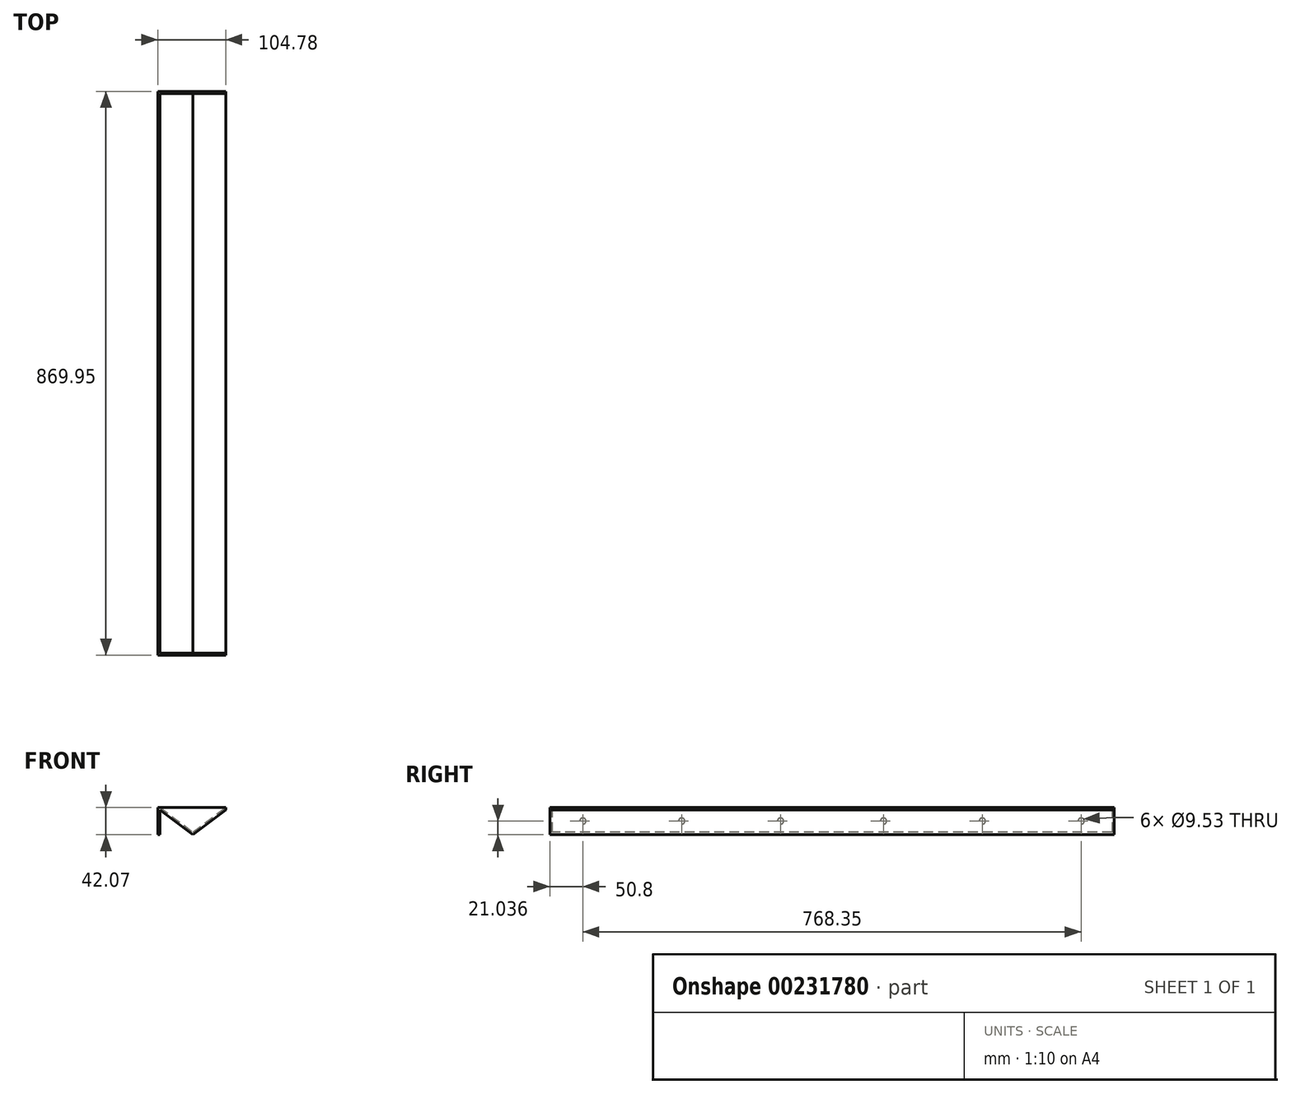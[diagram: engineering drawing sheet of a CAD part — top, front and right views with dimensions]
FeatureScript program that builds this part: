
annotation { "Feature Type Name" : "Feature", "Feature Type Description" : "" }
export const myFeature = defineFeature(function(context is Context, id is Id, definition is map)
    precondition{}
    {
        {
            var Q0;
            Q0=qCreatedBy(makeId("Front.planeOp"),FACE);
            var sketch = newSketch(context, id + "F0", { "sketchPlane" : qUnion([Q0])});
            skLineSegment(sketch, "E0", {"start": v(-50.8, 0) * mm, "end": v(50.8, 0) * mm, "construction": true});
            skLineSegment(sketch, "E1", {"start": v(-50.8, 0) * mm, "end": v(0, -38.1) * mm});
            skLineSegment(sketch, "E2", {"start": v(0, -38.1) * mm, "end": v(50.8, 0) * mm});
            skLineSegment(sketch, "E3", {"start": v(-50.8, 0) * mm, "end": v(-50.8, -42.07) * mm});
            skLineSegment(sketch, "E4", {"start": v(-50.8, -42.07) * mm, "end": v(-53.97, -42.07) * mm});
            skLineSegment(sketch, "E5", {"start": v(-53.97, -42.07) * mm, "end": v(-53.97, 0) * mm});
            skLineSegment(sketch, "E6", {"start": v(-53.97, 0) * mm, "end": v(-50.8, 0) * mm});
            skLineSegment(sketch, "E7.0", {"start": v(-50.8, -3.97) * mm, "end": v(0, -42.07) * mm});
            skLineSegment(sketch, "E8.0", {"start": v(0, -42.07) * mm, "end": v(50.8, -3.97) * mm});
            skLineSegment(sketch, "E9", {"start": v(0, -38.1) * mm, "end": v(0, -46.2) * mm, "construction": true});
            skLineSegment(sketch, "E10", {"start": v(-50.8, 0) * mm, "end": v(-50.8, -3.97) * mm});
            skLineSegment(sketch, "E11", {"start": v(50.8, -3.97) * mm, "end": v(50.8, 0) * mm});
            skLineSegment(sketch, "E12", {"start": v(0, -42.07) * mm, "end": v(-53.97, -42.07) * mm, "construction": true});
            skSolve(sketch);
        }
        {
            var Q0;
            Q0=makeQuery(id+"F0.imprint","IMPRINT",FACE,{"disambiguationData":[TD([[makeQuery(id+"F0.imprint","IMPRINT",EDGE,{"derivedFrom":sQuery(id+"F0.wireOp",EDGE,"E1")}),-1.0]])]});
            var Q1;
            Q1=makeQuery(id+"F0.imprint","IMPRINT",FACE,{"disambiguationData":[TD([[makeQuery(id+"F0.imprint","IMPRINT",EDGE,{"derivedFrom":sQuery(id+"F0.wireOp",EDGE,"E3")}),-1.0]])]});
            extrude(context, id + "F1", {"entities" : qUnion([Q0, Q1]), "oppositeDirection" : true, "depth" : 869.95 * mm});
        }
        {
            var Q0;
            Q0=makeQuery(id+"F1.opExtrude","CAP_FACE",FACE,{"disambiguationData":[OSD([sQuery(id+"F0.wireOp",EDGE,"E1"),sQuery(id+"F0.wireOp",EDGE,"E2"),sQuery(id+"F0.wireOp",EDGE,"E3"),sQuery(id+"F0.wireOp",EDGE,"E4"),sQuery(id+"F0.wireOp",EDGE,"E5"),sQuery(id+"F0.wireOp",EDGE,"E6"),sQuery(id+"F0.wireOp",EDGE,"E7.0"),sQuery(id+"F0.wireOp",EDGE,"E8.0"),sQuery(id+"F0.wireOp",EDGE,"E11")])],"isStart":false});
            var sketch = newSketch(context, id + "F2", { "sketchPlane" : qUnion([Q0])});
            skLineSegment(sketch, "E13", {"start": v(-50.8, 0) * mm, "end": v(50.8, 0) * mm});
            skLineSegment(sketch, "E14", {"start": v(50.8, 0) * mm, "end": v(50.8, -3.97) * mm});
            skLineSegment(sketch, "E15", {"start": v(50.8, -3.97) * mm, "end": v(0, -42.07) * mm});
            skLineSegment(sketch, "E16", {"start": v(0, -42.07) * mm, "end": v(-50.8, -3.97) * mm});
            skLineSegment(sketch, "E17", {"start": v(-50.8, -3.97) * mm, "end": v(-50.8, 0) * mm});
            skSolve(sketch);
        }
        {
            var Q0;
            Q0=makeQuery(id+"F2.imprint","IMPRINT",FACE,{"disambiguationData":[TD([[makeQuery(id+"F2.imprint","IMPRINT",EDGE,{"derivedFrom":sQuery(id+"F2.wireOp",EDGE,"E13")}),-1.0]])]});
            extrude(context, id + "F3", {"entities" : qUnion([Q0]), "operationType" : NewBodyOperationType.ADD, "oppositeDirection" : true, "depth" : 3.17 * mm});
        }
        {
            var Q0;
            Q0=makeQuery(id+"F1.opExtrude","CAP_FACE",FACE,{"disambiguationData":[OSD([sQuery(id+"F0.wireOp",EDGE,"E1"),sQuery(id+"F0.wireOp",EDGE,"E2"),sQuery(id+"F0.wireOp",EDGE,"E3"),sQuery(id+"F0.wireOp",EDGE,"E4"),sQuery(id+"F0.wireOp",EDGE,"E5"),sQuery(id+"F0.wireOp",EDGE,"E6"),sQuery(id+"F0.wireOp",EDGE,"E7.0"),sQuery(id+"F0.wireOp",EDGE,"E8.0"),sQuery(id+"F0.wireOp",EDGE,"E11")])],"isStart":true});
            var sketch = newSketch(context, id + "F4", { "sketchPlane" : qUnion([Q0])});
            skLineSegment(sketch, "E18", {"start": v(-50.8, 0) * mm, "end": v(50.8, 0) * mm});
            skLineSegment(sketch, "E19", {"start": v(50.8, 0) * mm, "end": v(0, -38.1) * mm});
            skLineSegment(sketch, "E20", {"start": v(0, -38.1) * mm, "end": v(-50.8, 0) * mm});
            skSolve(sketch);
        }
        {
            var Q0;
            Q0=makeQuery(id+"F4.imprint","IMPRINT",FACE,{"disambiguationData":[TD([[makeQuery(id+"F4.imprint","IMPRINT",EDGE,{"derivedFrom":sQuery(id+"F4.wireOp",EDGE,"E18")}),-1.0]])]});
            extrude(context, id + "F5", {"entities" : qUnion([Q0]), "operationType" : NewBodyOperationType.ADD, "oppositeDirection" : true, "depth" : 3.17 * mm});
        }
        {
            var Q0;
            Q0=makeQuery(id+"F1.opExtrude","SWEPT_FACE",FACE,{"disambiguationData":[OSD([sQuery(id+"F0.wireOp",EDGE,"E5")])]});
            var sketch = newSketch(context, id + "F6", { "sketchPlane" : qUnion([Q0])});
            skLineSegment(sketch, "E21", {"start": v(-869.95, -21.03) * mm, "end": v(0, -21.03) * mm, "construction": true});
            skCircle(sketch, "E22", {"center": v(-819.15, -21.03) * mm, "radius": 4.76 * mm});
            skLineSegment(sketch, "E23.direction1", {"start": v(-819.15, -21.03) * mm, "end": v(-621.28, -21.03) * mm, "construction": true});
            skCircle(sketch, "E24", {"center": v(-50.8, -21.03) * mm, "radius": 4.76 * mm});
            skLineSegment(sketch, "E25", {"start": v(-434.98, 0) * mm, "end": v(-434.98, -42.07) * mm, "construction": true});
            skCircle(sketch, "E26", {"center": v(-666.75, -21.03) * mm, "radius": 4.76 * mm});
            skCircle(sketch, "E27", {"center": v(-203.2, -21.03) * mm, "radius": 4.76 * mm});
            skCircle(sketch, "E28", {"center": v(-514.35, -21.03) * mm, "radius": 4.76 * mm});
            skCircle(sketch, "E29", {"center": v(-355.6, -21.03) * mm, "radius": 4.76 * mm});
            skSolve(sketch);
        }
        {
            var Q0;
            Q0=sQuery(id+"F6.wireOp",VERTEX,"E22.center");
            var Q1;
            Q1=sQuery(id+"F6.wireOp",VERTEX,"E26.center");
            var Q2;
            Q2=sQuery(id+"F6.wireOp",VERTEX,"E28.center");
            var Q3;
            Q3=sQuery(id+"F6.wireOp",VERTEX,"E29.center");
            var Q4;
            Q4=sQuery(id+"F6.wireOp",VERTEX,"E27.center");
            var Q5;
            Q5=sQuery(id+"F6.wireOp",VERTEX,"E24.center");
            var Q6;
            Q6=makeQuery(id+"F1.opExtrude","SWEPT_BODY",BODY,{"disambiguationData":[OSD([sQuery(id+"F0.wireOp",EDGE,"E1"),sQuery(id+"F0.wireOp",EDGE,"E2"),sQuery(id+"F0.wireOp",EDGE,"E3"),sQuery(id+"F0.wireOp",EDGE,"E4"),sQuery(id+"F0.wireOp",EDGE,"E5"),sQuery(id+"F0.wireOp",EDGE,"E6"),sQuery(id+"F0.wireOp",EDGE,"E7.0"),sQuery(id+"F0.wireOp",EDGE,"E8.0"),sQuery(id+"F0.wireOp",EDGE,"E11")])]});
            hole(context, id + "F7", {"style" : HoleStyle.SIMPLE, "endStyle" : HoleEndStyle.BLIND, "holeDiameter" : 9.52 * mm, "holeDepth" : 5.08 * mm, "locations" : qUnion([Q0, Q1, Q2, Q3, Q4, Q5]), "scope" : qUnion([Q6])});
        }
    });
